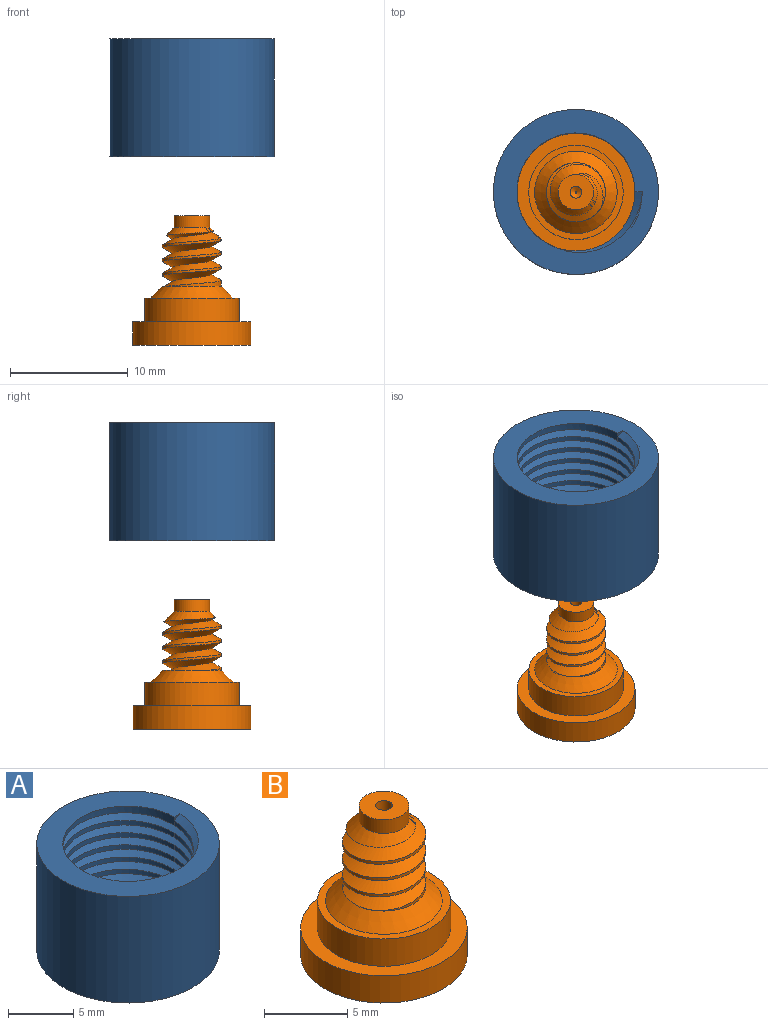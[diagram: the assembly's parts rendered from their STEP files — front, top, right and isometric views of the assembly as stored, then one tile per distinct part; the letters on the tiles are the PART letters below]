
ASSEMBLY  parts=2 mates=1
PART A: 15 faces, bbox 14.3x14.3x10.7 mm
  f0: cylinder r=5mm len=10mm, axis (0,0,-1), area 8.4mm2, adj f1,f9,f11,f14
  f1: cylinder r=5mm len=10mm, axis (0,0,-1), area 13.3mm2, adj f0,f2,f13,f14
  f2: cylinder r=5mm len=10mm, axis (0,0,-1), area 13.3mm2, adj f1,f3,f13,f14
  f3: cylinder r=5mm len=10mm, axis (0,0,-1), area 13.2mm2, adj f2,f4,f13,f14
  f4: cylinder r=5mm len=10mm, axis (0,0,-1), area 13.2mm2, adj f3,f5,f13,f14
  f5: cylinder r=5mm len=10mm, axis (0,0,-1), area 13.3mm2, adj f4,f6,f13,f14
  f6: cylinder r=5mm len=10mm, axis (0,0,-1), area 13.2mm2, adj f5,f7,f13,f14
  f7: cylinder r=5mm len=10mm, axis (0,0,-1), area 69.5mm2, adj f6,f10,f12,f13
  f8: cylinder r=7mm len=14mm, axis (0,0,-1), area 439.8mm2, adj f9,f10
  f9: plane 14.34x14.34mm, normal (0,0,1), area 72.2mm2, adj f0,f8,f11,f14
  f10: plane 14x14mm, normal (0,0,-1), area 75.4mm2, adj f7,f8
  f11: plane 0.62x0.36mm, normal (0,-1,0), area 0.1mm2, adj f0,f9,f13
  f12: plane 0.72x0.62mm, normal (0,1,0), area 0.2mm2, adj f7,f13,f14
  f13: bspline ~12.99x11.25mm, area 168.4mm2, adj f1,f2,f3,f4,f5,f6,f7,f11
  f14: bspline ~12.99x11.25mm, area 164.8mm2, adj f0,f1,f2,f3,f4,f5,f6,f9
PART B: 17 faces, bbox 10x10x11 mm
  f0: cylinder r=2.5mm len=5mm, axis (0,0,-1), area 10.8mm2, adj f11,f12,f14,f15,f16
  f1: cone r=0mm half-angle=59deg, axis (0,0,1), area 0.9mm2, adj f9,f10
  f2: plane 8x8mm, normal (0,0,1), area 11.8mm2, adj f3,f11
  f3: cylinder r=4mm len=8mm, axis (0,0,-1), area 50.3mm2, adj f2,f4
  f4: plane 10x10mm, normal (0,0,1), area 28.3mm2, adj f3,f5
  f5: cylinder r=5mm len=10mm, axis (0,0,-1), area 62.8mm2, adj f4,f6
  f6: plane 10x10mm, normal (0,0,-1), area 78.5mm2, adj f5,f10
  f7: plane 3x3mm, normal (0,0,1), area 6.3mm2, adj f8,f9
  f8: cylinder r=1.5mm len=3mm, axis (0,0,-1), area 9.4mm2, adj f7,f12
  f9: cylinder r=0.5mm len=10mm, axis (0,0,1), area 31.4mm2, adj f1,f7
  f10: cylinder r=0.05mm len=0.73mm, axis (0,0,-1), area 0.2mm2, adj f1,f6
  f11: cone r=3.5mm half-angle=45deg, axis (0,0,-1), area 26.7mm2, adj f0,f2,f13
  f12: cone r=2.5mm half-angle=45deg, axis (0,0,-1), area 10.7mm2, adj f0,f8,f15,f16
  f13: cylinder r=2.5mm len=5mm, axis (0,0,1), area 3.2mm2, adj f11,f14,f15
  f14: plane 1x0.87mm, normal (0,1,0), area 0.4mm2, adj f0,f13,f15,f16
  f15: bspline ~5.77x5.7mm, area 52.9mm2, adj f0,f12,f13,f14,f16
  f16: bspline ~5.77x5.7mm, area 48.5mm2, adj f0,f12,f14,f15
PLACE A t=(-10.42,-13.81,2.45)mm
PLACE B t=(-10.42,-13.81,-13.55)mm
MATE parallel B.f0 <-> A.f0  axis (0,0,-1) through (-10.42,-13.81,-13.55)mm
